# Revit family: vanity unit with 4 drawers for consoles with bowl
name_source: partatom
category: Furniture
units: mm (PartAtom-declared; Revit-internal decimal feet)

## family parameters
Always vertical = Yes
Cut with Voids When Loaded = No
OmniClass Number = 23.21.19.15.33.13
Room Calculation Point = No
Shared = Yes
Work Plane-Based = No

## types (48) — shared parameters
BIMOBJECT = Sanitary: Compound units
CATALOG = Hansgrohe
DESIGN = Germany
ETIM = EC011381 | Bathroom furniture set
IFC = Furnishing element
MASTERFORMAT = 12 35 30.23 | Bathroom Casework
Manufacturer = Hansgrohe
NBSYN = $BASENUMBER.-$ARTNR.-$OBERFLAECHE.-$SURFACE.-$LODLEVEL.
NN = Vanity Unit with 4 Drawers for consoles with bowl
OBJECTTYPE = Object (single object)
OMNICLASS = 23-21 19 15 33 13 | Residential Bathroom Specialty Casework
PRODUCTFAMILY = Xelu Q
PRODUCTGROUP = vanity unit
PRODUCTURL = https://pro.hansgrohe.com
REGIONSET = Worldwide
UNICLASS2015 = Pr_40_30_78_05 | Bathroom furniture
UNICLASS_2015_CODE = 40_30_78_05
UNIFORMATII = E2010 | Fixed Furnishings
UNSPSC = 56 | Furniture and Furnishings
etim7_EC011381 = EC011381

## per-type parameters (varying)
| type | ARTNR | BASENUMBER | GTINCODE | L | LINA | LODLEVEL | Model | NAME | NB | OBERFLAECHE | PERMALINK | SURFACE | WEIGHT |
| Vanity unit 1360_550 with 4 drawers for consoles with bowl-54086000-High Gloss White-CHROME-200 | 54086000 | Vanity unit 1360/550 with 4 drawers for consoles with bowl | 4059625456972 | 1360 | Vanity unit 1360/550 with 4 drawers for consoles with bowl-54086000-High Gloss White-CHROME-200 | 200 | Vanity unit 1360/550 with 4 drawers for consoles with bowl-54086000-High Gloss White-CHROME-200 | Xelu Q Vanity unit High Gloss White 1360/550 with 4 drawers for consoles with bowl | Vanity unit 1360/550 with 4 drawers for consoles with bowl-54086000-High Gloss White-CHROME-200 | High Gloss White | 54086XXX | CHROME | 55.8 |
| Vanity unit 1360_550 with 4 drawers for consoles with bowl-54086000-High Gloss White-CHROME-400 | 54086000 | Vanity unit 1360/550 with 4 drawers for consoles with bowl | 4059625456972 | 1360 | Vanity unit 1360/550 with 4 drawers for consoles with bowl-54086000-High Gloss White-CHROME-400 | 400 | Vanity unit 1360/550 with 4 drawers for consoles with bowl-54086000-High Gloss White-CHROME-400 | Xelu Q Vanity unit High Gloss White 1360/550 with 4 drawers for consoles with bowl | Vanity unit 1360/550 with 4 drawers for consoles with bowl-54086000-High Gloss White-CHROME-400 | High Gloss White | 54086XXX | CHROME | 55.8 |
| Vanity unit 1360_550 with 4 drawers for consoles with bowl-54086670-High Gloss White-MATT_BLACK-200 | 54086670 | Vanity unit 1360/550 with 4 drawers for consoles with bowl | 4059625456972 | 1360 | Vanity unit 1360/550 with 4 drawers for consoles with bowl-54086670-High Gloss White-MATT_BLACK-200 | 200 | Vanity unit 1360/550 with 4 drawers for consoles with bowl-54086670-High Gloss White-MATT_BLACK-200 | Xelu Q Vanity unit High Gloss White 1360/550 with 4 drawers for consoles with bowl | Vanity unit 1360/550 with 4 drawers for consoles with bowl-54086670-High Gloss White-MATT_BLACK-200 | High Gloss White | 54086XXX | MATT_BLACK | 55.8 |
| Vanity unit 1360_550 with 4 drawers for consoles with bowl-54086670-High Gloss White-MATT_BLACK-400 | 54086670 | Vanity unit 1360/550 with 4 drawers for consoles with bowl | 4059625456972 | 1360 | Vanity unit 1360/550 with 4 drawers for consoles with bowl-54086670-High Gloss White-MATT_BLACK-400 | 400 | Vanity unit 1360/550 with 4 drawers for consoles with bowl-54086670-High Gloss White-MATT_BLACK-400 | Xelu Q Vanity unit High Gloss White 1360/550 with 4 drawers for consoles with bowl | Vanity unit 1360/550 with 4 drawers for consoles with bowl-54086670-High Gloss White-MATT_BLACK-400 | High Gloss White | 54086XXX | MATT_BLACK | 55.8 |
| Vanity unit 1360_550 with 4 drawers for consoles with bowl-54086700-High Gloss White-MATT_WHITE-200 | 54086700 | Vanity unit 1360/550 with 4 drawers for consoles with bowl | 4059625456972 | 1360 | Vanity unit 1360/550 with 4 drawers for consoles with bowl-54086700-High Gloss White-MATT_WHITE-200 | 200 | Vanity unit 1360/550 with 4 drawers for consoles with bowl-54086700-High Gloss White-MATT_WHITE-200 | Xelu Q Vanity unit High Gloss White 1360/550 with 4 drawers for consoles with bowl | Vanity unit 1360/550 with 4 drawers for consoles with bowl-54086700-High Gloss White-MATT_WHITE-200 | High Gloss White | 54086XXX | MATT_WHITE | 55.8 |
| Vanity unit 1360_550 with 4 drawers for consoles with bowl-54086700-High Gloss White-MATT_WHITE-400 | 54086700 | Vanity unit 1360/550 with 4 drawers for consoles with bowl | 4059625456972 | 1360 | Vanity unit 1360/550 with 4 drawers for consoles with bowl-54086700-High Gloss White-MATT_WHITE-400 | 400 | Vanity unit 1360/550 with 4 drawers for consoles with bowl-54086700-High Gloss White-MATT_WHITE-400 | Xelu Q Vanity unit High Gloss White 1360/550 with 4 drawers for consoles with bowl | Vanity unit 1360/550 with 4 drawers for consoles with bowl-54086700-High Gloss White-MATT_WHITE-400 | High Gloss White | 54086XXX | MATT_WHITE | 55.8 |
| Vanity unit 1360_550 with 4 drawers for consoles with bowl-54087000-Diamond Matt Grey-CHROME-200 | 54087000 | Vanity unit 1360/550 with 4 drawers for consoles with bowl | 4059625456941 | 1360 | Vanity unit 1360/550 with 4 drawers for consoles with bowl-54087000-Diamond Matt Grey-CHROME-200 | 200 | Vanity unit 1360/550 with 4 drawers for consoles with bowl-54087000-Diamond Matt Grey-CHROME-200 | Xelu Q Vanity unit Diamond Matt Grey 1360/550 with 4 drawers for consoles with bowl | Vanity unit 1360/550 with 4 drawers for consoles with bowl-54087000-Diamond Matt Grey-CHROME-200 | Diamond Matt Grey | 54087XXX | CHROME | 55.8 |
| Vanity unit 1360_550 with 4 drawers for consoles with bowl-54087000-Diamond Matt Grey-CHROME-400 | 54087000 | Vanity unit 1360/550 with 4 drawers for consoles with bowl | 4059625456941 | 1360 | Vanity unit 1360/550 with 4 drawers for consoles with bowl-54087000-Diamond Matt Grey-CHROME-400 | 400 | Vanity unit 1360/550 with 4 drawers for consoles with bowl-54087000-Diamond Matt Grey-CHROME-400 | Xelu Q Vanity unit Diamond Matt Grey 1360/550 with 4 drawers for consoles with bowl | Vanity unit 1360/550 with 4 drawers for consoles with bowl-54087000-Diamond Matt Grey-CHROME-400 | Diamond Matt Grey | 54087XXX | CHROME | 55.8 |
| Vanity unit 1360_550 with 4 drawers for consoles with bowl-54087670-Diamond Matt Grey-MATT_BLACK-200 | 54087670 | Vanity unit 1360/550 with 4 drawers for consoles with bowl | 4059625456941 | 1360 | Vanity unit 1360/550 with 4 drawers for consoles with bowl-54087670-Diamond Matt Grey-MATT_BLACK-200 | 200 | Vanity unit 1360/550 with 4 drawers for consoles with bowl-54087670-Diamond Matt Grey-MATT_BLACK-200 | Xelu Q Vanity unit Diamond Matt Grey 1360/550 with 4 drawers for consoles with bowl | Vanity unit 1360/550 with 4 drawers for consoles with bowl-54087670-Diamond Matt Grey-MATT_BLACK-200 | Diamond Matt Grey | 54087XXX | MATT_BLACK | 55.8 |
| Vanity unit 1360_550 with 4 drawers for consoles with bowl-54087670-Diamond Matt Grey-MATT_BLACK-400 | 54087670 | Vanity unit 1360/550 with 4 drawers for consoles with bowl | 4059625456941 | 1360 | Vanity unit 1360/550 with 4 drawers for consoles with bowl-54087670-Diamond Matt Grey-MATT_BLACK-400 | 400 | Vanity unit 1360/550 with 4 drawers for consoles with bowl-54087670-Diamond Matt Grey-MATT_BLACK-400 | Xelu Q Vanity unit Diamond Matt Grey 1360/550 with 4 drawers for consoles with bowl | Vanity unit 1360/550 with 4 drawers for consoles with bowl-54087670-Diamond Matt Grey-MATT_BLACK-400 | Diamond Matt Grey | 54087XXX | MATT_BLACK | 55.8 |
| Vanity unit 1360_550 with 4 drawers for consoles with bowl-54087700-Diamond Matt Grey-MATT_WHITE-200 | 54087700 | Vanity unit 1360/550 with 4 drawers for consoles with bowl | 4059625456941 | 1360 | Vanity unit 1360/550 with 4 drawers for consoles with bowl-54087700-Diamond Matt Grey-MATT_WHITE-200 | 200 | Vanity unit 1360/550 with 4 drawers for consoles with bowl-54087700-Diamond Matt Grey-MATT_WHITE-200 | Xelu Q Vanity unit Diamond Matt Grey 1360/550 with 4 drawers for consoles with bowl | Vanity unit 1360/550 with 4 drawers for consoles with bowl-54087700-Diamond Matt Grey-MATT_WHITE-200 | Diamond Matt Grey | 54087XXX | MATT_WHITE | 55.8 |
| Vanity unit 1360_550 with 4 drawers for consoles with bowl-54087700-Diamond Matt Grey-MATT_WHITE-400 | 54087700 | Vanity unit 1360/550 with 4 drawers for consoles with bowl | 4059625456941 | 1360 | Vanity unit 1360/550 with 4 drawers for consoles with bowl-54087700-Diamond Matt Grey-MATT_WHITE-400 | 400 | Vanity unit 1360/550 with 4 drawers for consoles with bowl-54087700-Diamond Matt Grey-MATT_WHITE-400 | Xelu Q Vanity unit Diamond Matt Grey 1360/550 with 4 drawers for consoles with bowl | Vanity unit 1360/550 with 4 drawers for consoles with bowl-54087700-Diamond Matt Grey-MATT_WHITE-400 | Diamond Matt Grey | 54087XXX | MATT_WHITE | 55.8 |
| Vanity unit 1360_550 with 4 drawers for consoles with bowl-54088000-Natural Oak-CHROME-200 | 54088000 | Vanity unit 1360/550 with 4 drawers for consoles with bowl | 4059625456910 | 1360 | Vanity unit 1360/550 with 4 drawers for consoles with bowl-54088000-Natural Oak-CHROME-200 | 200 | Vanity unit 1360/550 with 4 drawers for consoles with bowl-54088000-Natural Oak-CHROME-200 | Xelu Q Vanity unit Natural Oak 1360/550 with 4 drawers for consoles with bowl | Vanity unit 1360/550 with 4 drawers for consoles with bowl-54088000-Natural Oak-CHROME-200 | Natural Oak | 54088XXX | CHROME | 55.8 |
| Vanity unit 1360_550 with 4 drawers for consoles with bowl-54088000-Natural Oak-CHROME-400 | 54088000 | Vanity unit 1360/550 with 4 drawers for consoles with bowl | 4059625456910 | 1360 | Vanity unit 1360/550 with 4 drawers for consoles with bowl-54088000-Natural Oak-CHROME-400 | 400 | Vanity unit 1360/550 with 4 drawers for consoles with bowl-54088000-Natural Oak-CHROME-400 | Xelu Q Vanity unit Natural Oak 1360/550 with 4 drawers for consoles with bowl | Vanity unit 1360/550 with 4 drawers for consoles with bowl-54088000-Natural Oak-CHROME-400 | Natural Oak | 54088XXX | CHROME | 55.8 |
| Vanity unit 1360_550 with 4 drawers for consoles with bowl-54088670-Natural Oak-MATT_BLACK-200 | 54088670 | Vanity unit 1360/550 with 4 drawers for consoles with bowl | 4059625456910 | 1360 | Vanity unit 1360/550 with 4 drawers for consoles with bowl-54088670-Natural Oak-MATT_BLACK-200 | 200 | Vanity unit 1360/550 with 4 drawers for consoles with bowl-54088670-Natural Oak-MATT_BLACK-200 | Xelu Q Vanity unit Natural Oak 1360/550 with 4 drawers for consoles with bowl | Vanity unit 1360/550 with 4 drawers for consoles with bowl-54088670-Natural Oak-MATT_BLACK-200 | Natural Oak | 54088XXX | MATT_BLACK | 55.8 |
| Vanity unit 1360_550 with 4 drawers for consoles with bowl-54088670-Natural Oak-MATT_BLACK-400 | 54088670 | Vanity unit 1360/550 with 4 drawers for consoles with bowl | 4059625456910 | 1360 | Vanity unit 1360/550 with 4 drawers for consoles with bowl-54088670-Natural Oak-MATT_BLACK-400 | 400 | Vanity unit 1360/550 with 4 drawers for consoles with bowl-54088670-Natural Oak-MATT_BLACK-400 | Xelu Q Vanity unit Natural Oak 1360/550 with 4 drawers for consoles with bowl | Vanity unit 1360/550 with 4 drawers for consoles with bowl-54088670-Natural Oak-MATT_BLACK-400 | Natural Oak | 54088XXX | MATT_BLACK | 55.8 |
| Vanity unit 1360_550 with 4 drawers for consoles with bowl-54088700-Natural Oak-MATT_WHITE-200 | 54088700 | Vanity unit 1360/550 with 4 drawers for consoles with bowl | 4059625456910 | 1360 | Vanity unit 1360/550 with 4 drawers for consoles with bowl-54088700-Natural Oak-MATT_WHITE-200 | 200 | Vanity unit 1360/550 with 4 drawers for consoles with bowl-54088700-Natural Oak-MATT_WHITE-200 | Xelu Q Vanity unit Natural Oak 1360/550 with 4 drawers for consoles with bowl | Vanity unit 1360/550 with 4 drawers for consoles with bowl-54088700-Natural Oak-MATT_WHITE-200 | Natural Oak | 54088XXX | MATT_WHITE | 55.8 |
| Vanity unit 1360_550 with 4 drawers for consoles with bowl-54088700-Natural Oak-MATT_WHITE-400 | 54088700 | Vanity unit 1360/550 with 4 drawers for consoles with bowl | 4059625456910 | 1360 | Vanity unit 1360/550 with 4 drawers for consoles with bowl-54088700-Natural Oak-MATT_WHITE-400 | 400 | Vanity unit 1360/550 with 4 drawers for consoles with bowl-54088700-Natural Oak-MATT_WHITE-400 | Xelu Q Vanity unit Natural Oak 1360/550 with 4 drawers for consoles with bowl | Vanity unit 1360/550 with 4 drawers for consoles with bowl-54088700-Natural Oak-MATT_WHITE-400 | Natural Oak | 54088XXX | MATT_WHITE | 55.8 |
| Vanity unit 1360_550 with 4 drawers for consoles with bowl-54089000-Dark Walnut-CHROME-200 | 54089000 | Vanity unit 1360/550 with 4 drawers for consoles with bowl | 4059625456880 | 1360 | Vanity unit 1360/550 with 4 drawers for consoles with bowl-54089000-Dark Walnut-CHROME-200 | 200 | Vanity unit 1360/550 with 4 drawers for consoles with bowl-54089000-Dark Walnut-CHROME-200 | Xelu Q Vanity unit Dark Walnut 1360/550 with 4 drawers for consoles with bowl | Vanity unit 1360/550 with 4 drawers for consoles with bowl-54089000-Dark Walnut-CHROME-200 | Dark Walnut | 54089XXX | CHROME | 55.8 |
| Vanity unit 1360_550 with 4 drawers for consoles with bowl-54089000-Dark Walnut-CHROME-400 | 54089000 | Vanity unit 1360/550 with 4 drawers for consoles with bowl | 4059625456880 | 1360 | Vanity unit 1360/550 with 4 drawers for consoles with bowl-54089000-Dark Walnut-CHROME-400 | 400 | Vanity unit 1360/550 with 4 drawers for consoles with bowl-54089000-Dark Walnut-CHROME-400 | Xelu Q Vanity unit Dark Walnut 1360/550 with 4 drawers for consoles with bowl | Vanity unit 1360/550 with 4 drawers for consoles with bowl-54089000-Dark Walnut-CHROME-400 | Dark Walnut | 54089XXX | CHROME | 55.8 |
| Vanity unit 1360_550 with 4 drawers for consoles with bowl-54089670-Dark Walnut-MATT_BLACK-200 | 54089670 | Vanity unit 1360/550 with 4 drawers for consoles with bowl | 4059625456880 | 1360 | Vanity unit 1360/550 with 4 drawers for consoles with bowl-54089670-Dark Walnut-MATT_BLACK-200 | 200 | Vanity unit 1360/550 with 4 drawers for consoles with bowl-54089670-Dark Walnut-MATT_BLACK-200 | Xelu Q Vanity unit Dark Walnut 1360/550 with 4 drawers for consoles with bowl | Vanity unit 1360/550 with 4 drawers for consoles with bowl-54089670-Dark Walnut-MATT_BLACK-200 | Dark Walnut | 54089XXX | MATT_BLACK | 55.8 |
| Vanity unit 1360_550 with 4 drawers for consoles with bowl-54089670-Dark Walnut-MATT_BLACK-400 | 54089670 | Vanity unit 1360/550 with 4 drawers for consoles with bowl | 4059625456880 | 1360 | Vanity unit 1360/550 with 4 drawers for consoles with bowl-54089670-Dark Walnut-MATT_BLACK-400 | 400 | Vanity unit 1360/550 with 4 drawers for consoles with bowl-54089670-Dark Walnut-MATT_BLACK-400 | Xelu Q Vanity unit Dark Walnut 1360/550 with 4 drawers for consoles with bowl | Vanity unit 1360/550 with 4 drawers for consoles with bowl-54089670-Dark Walnut-MATT_BLACK-400 | Dark Walnut | 54089XXX | MATT_BLACK | 55.8 |
| Vanity unit 1360_550 with 4 drawers for consoles with bowl-54089700-Dark Walnut-MATT_WHITE-200 | 54089700 | Vanity unit 1360/550 with 4 drawers for consoles with bowl | 4059625456880 | 1360 | Vanity unit 1360/550 with 4 drawers for consoles with bowl-54089700-Dark Walnut-MATT_WHITE-200 | 200 | Vanity unit 1360/550 with 4 drawers for consoles with bowl-54089700-Dark Walnut-MATT_WHITE-200 | Xelu Q Vanity unit Dark Walnut 1360/550 with 4 drawers for consoles with bowl | Vanity unit 1360/550 with 4 drawers for consoles with bowl-54089700-Dark Walnut-MATT_WHITE-200 | Dark Walnut | 54089XXX | MATT_WHITE | 55.8 |
| Vanity unit 1360_550 with 4 drawers for consoles with bowl-54089700-Dark Walnut-MATT_WHITE-400 | 54089700 | Vanity unit 1360/550 with 4 drawers for consoles with bowl | 4059625456880 | 1360 | Vanity unit 1360/550 with 4 drawers for consoles with bowl-54089700-Dark Walnut-MATT_WHITE-400 | 400 | Vanity unit 1360/550 with 4 drawers for consoles with bowl-54089700-Dark Walnut-MATT_WHITE-400 | Xelu Q Vanity unit Dark Walnut 1360/550 with 4 drawers for consoles with bowl | Vanity unit 1360/550 with 4 drawers for consoles with bowl-54089700-Dark Walnut-MATT_WHITE-400 | Dark Walnut | 54089XXX | MATT_WHITE | 55.8 |
| Vanity unit 1560_550 with 4 drawers for consoles with bowl-54090000-High Gloss White-CHROME-200 | 54090000 | Vanity unit 1560/550 with 4 drawers for consoles with bowl | 4059625456859 | 1560 | Vanity unit 1560/550 with 4 drawers for consoles with bowl-54090000-High Gloss White-CHROME-200 | 200 | Vanity unit 1560/550 with 4 drawers for consoles with bowl-54090000-High Gloss White-CHROME-200 | Xelu Q Vanity unit High Gloss White 1560/550 with 4 drawers for consoles with bowl | Vanity unit 1560/550 with 4 drawers for consoles with bowl-54090000-High Gloss White-CHROME-200 | High Gloss White | 54090XXX | CHROME | 61 |
| Vanity unit 1560_550 with 4 drawers for consoles with bowl-54090000-High Gloss White-CHROME-400 | 54090000 | Vanity unit 1560/550 with 4 drawers for consoles with bowl | 4059625456859 | 1560 | Vanity unit 1560/550 with 4 drawers for consoles with bowl-54090000-High Gloss White-CHROME-400 | 400 | Vanity unit 1560/550 with 4 drawers for consoles with bowl-54090000-High Gloss White-CHROME-400 | Xelu Q Vanity unit High Gloss White 1560/550 with 4 drawers for consoles with bowl | Vanity unit 1560/550 with 4 drawers for consoles with bowl-54090000-High Gloss White-CHROME-400 | High Gloss White | 54090XXX | CHROME | 61 |
| Vanity unit 1560_550 with 4 drawers for consoles with bowl-54090670-High Gloss White-MATT_BLACK-200 | 54090670 | Vanity unit 1560/550 with 4 drawers for consoles with bowl | 4059625456859 | 1560 | Vanity unit 1560/550 with 4 drawers for consoles with bowl-54090670-High Gloss White-MATT_BLACK-200 | 200 | Vanity unit 1560/550 with 4 drawers for consoles with bowl-54090670-High Gloss White-MATT_BLACK-200 | Xelu Q Vanity unit High Gloss White 1560/550 with 4 drawers for consoles with bowl | Vanity unit 1560/550 with 4 drawers for consoles with bowl-54090670-High Gloss White-MATT_BLACK-200 | High Gloss White | 54090XXX | MATT_BLACK | 61 |
| Vanity unit 1560_550 with 4 drawers for consoles with bowl-54090670-High Gloss White-MATT_BLACK-400 | 54090670 | Vanity unit 1560/550 with 4 drawers for consoles with bowl | 4059625456859 | 1560 | Vanity unit 1560/550 with 4 drawers for consoles with bowl-54090670-High Gloss White-MATT_BLACK-400 | 400 | Vanity unit 1560/550 with 4 drawers for consoles with bowl-54090670-High Gloss White-MATT_BLACK-400 | Xelu Q Vanity unit High Gloss White 1560/550 with 4 drawers for consoles with bowl | Vanity unit 1560/550 with 4 drawers for consoles with bowl-54090670-High Gloss White-MATT_BLACK-400 | High Gloss White | 54090XXX | MATT_BLACK | 61 |
| Vanity unit 1560_550 with 4 drawers for consoles with bowl-54090700-High Gloss White-MATT_WHITE-200 | 54090700 | Vanity unit 1560/550 with 4 drawers for consoles with bowl | 4059625456859 | 1560 | Vanity unit 1560/550 with 4 drawers for consoles with bowl-54090700-High Gloss White-MATT_WHITE-200 | 200 | Vanity unit 1560/550 with 4 drawers for consoles with bowl-54090700-High Gloss White-MATT_WHITE-200 | Xelu Q Vanity unit High Gloss White 1560/550 with 4 drawers for consoles with bowl | Vanity unit 1560/550 with 4 drawers for consoles with bowl-54090700-High Gloss White-MATT_WHITE-200 | High Gloss White | 54090XXX | MATT_WHITE | 61 |
| Vanity unit 1560_550 with 4 drawers for consoles with bowl-54090700-High Gloss White-MATT_WHITE-400 | 54090700 | Vanity unit 1560/550 with 4 drawers for consoles with bowl | 4059625456859 | 1560 | Vanity unit 1560/550 with 4 drawers for consoles with bowl-54090700-High Gloss White-MATT_WHITE-400 | 400 | Vanity unit 1560/550 with 4 drawers for consoles with bowl-54090700-High Gloss White-MATT_WHITE-400 | Xelu Q Vanity unit High Gloss White 1560/550 with 4 drawers for consoles with bowl | Vanity unit 1560/550 with 4 drawers for consoles with bowl-54090700-High Gloss White-MATT_WHITE-400 | High Gloss White | 54090XXX | MATT_WHITE | 61 |
| Vanity unit 1560_550 with 4 drawers for consoles with bowl-54091000-Diamond Matt Grey-CHROME-200 | 54091000 | Vanity unit 1560/550 with 4 drawers for consoles with bowl | 4059625457221 | 1560 | Vanity unit 1560/550 with 4 drawers for consoles with bowl-54091000-Diamond Matt Grey-CHROME-200 | 200 | Vanity unit 1560/550 with 4 drawers for consoles with bowl-54091000-Diamond Matt Grey-CHROME-200 | Xelu Q Vanity unit Diamond Matt Grey 1560/550 with 4 drawers for consoles with bowl | Vanity unit 1560/550 with 4 drawers for consoles with bowl-54091000-Diamond Matt Grey-CHROME-200 | Diamond Matt Grey | 54091XXX | CHROME | 61 |
| Vanity unit 1560_550 with 4 drawers for consoles with bowl-54091000-Diamond Matt Grey-CHROME-400 | 54091000 | Vanity unit 1560/550 with 4 drawers for consoles with bowl | 4059625457221 | 1560 | Vanity unit 1560/550 with 4 drawers for consoles with bowl-54091000-Diamond Matt Grey-CHROME-400 | 400 | Vanity unit 1560/550 with 4 drawers for consoles with bowl-54091000-Diamond Matt Grey-CHROME-400 | Xelu Q Vanity unit Diamond Matt Grey 1560/550 with 4 drawers for consoles with bowl | Vanity unit 1560/550 with 4 drawers for consoles with bowl-54091000-Diamond Matt Grey-CHROME-400 | Diamond Matt Grey | 54091XXX | CHROME | 61 |
| Vanity unit 1560_550 with 4 drawers for consoles with bowl-54091670-Diamond Matt Grey-MATT_BLACK-200 | 54091670 | Vanity unit 1560/550 with 4 drawers for consoles with bowl | 4059625457221 | 1560 | Vanity unit 1560/550 with 4 drawers for consoles with bowl-54091670-Diamond Matt Grey-MATT_BLACK-200 | 200 | Vanity unit 1560/550 with 4 drawers for consoles with bowl-54091670-Diamond Matt Grey-MATT_BLACK-200 | Xelu Q Vanity unit Diamond Matt Grey 1560/550 with 4 drawers for consoles with bowl | Vanity unit 1560/550 with 4 drawers for consoles with bowl-54091670-Diamond Matt Grey-MATT_BLACK-200 | Diamond Matt Grey | 54091XXX | MATT_BLACK | 61 |
| Vanity unit 1560_550 with 4 drawers for consoles with bowl-54091670-Diamond Matt Grey-MATT_BLACK-400 | 54091670 | Vanity unit 1560/550 with 4 drawers for consoles with bowl | 4059625457221 | 1560 | Vanity unit 1560/550 with 4 drawers for consoles with bowl-54091670-Diamond Matt Grey-MATT_BLACK-400 | 400 | Vanity unit 1560/550 with 4 drawers for consoles with bowl-54091670-Diamond Matt Grey-MATT_BLACK-400 | Xelu Q Vanity unit Diamond Matt Grey 1560/550 with 4 drawers for consoles with bowl | Vanity unit 1560/550 with 4 drawers for consoles with bowl-54091670-Diamond Matt Grey-MATT_BLACK-400 | Diamond Matt Grey | 54091XXX | MATT_BLACK | 61 |
| Vanity unit 1560_550 with 4 drawers for consoles with bowl-54091700-Diamond Matt Grey-MATT_WHITE-200 | 54091700 | Vanity unit 1560/550 with 4 drawers for consoles with bowl | 4059625457221 | 1560 | Vanity unit 1560/550 with 4 drawers for consoles with bowl-54091700-Diamond Matt Grey-MATT_WHITE-200 | 200 | Vanity unit 1560/550 with 4 drawers for consoles with bowl-54091700-Diamond Matt Grey-MATT_WHITE-200 | Xelu Q Vanity unit Diamond Matt Grey 1560/550 with 4 drawers for consoles with bowl | Vanity unit 1560/550 with 4 drawers for consoles with bowl-54091700-Diamond Matt Grey-MATT_WHITE-200 | Diamond Matt Grey | 54091XXX | MATT_WHITE | 61 |
| Vanity unit 1560_550 with 4 drawers for consoles with bowl-54091700-Diamond Matt Grey-MATT_WHITE-400 | 54091700 | Vanity unit 1560/550 with 4 drawers for consoles with bowl | 4059625457221 | 1560 | Vanity unit 1560/550 with 4 drawers for consoles with bowl-54091700-Diamond Matt Grey-MATT_WHITE-400 | 400 | Vanity unit 1560/550 with 4 drawers for consoles with bowl-54091700-Diamond Matt Grey-MATT_WHITE-400 | Xelu Q Vanity unit Diamond Matt Grey 1560/550 with 4 drawers for consoles with bowl | Vanity unit 1560/550 with 4 drawers for consoles with bowl-54091700-Diamond Matt Grey-MATT_WHITE-400 | Diamond Matt Grey | 54091XXX | MATT_WHITE | 61 |
| Vanity unit 1560_550 with 4 drawers for consoles with bowl-54092000-Natural Oak-CHROME-200 | 54092000 | Vanity unit 1560/550 with 4 drawers for consoles with bowl | 4059625457191 | 1560 | Vanity unit 1560/550 with 4 drawers for consoles with bowl-54092000-Natural Oak-CHROME-200 | 200 | Vanity unit 1560/550 with 4 drawers for consoles with bowl-54092000-Natural Oak-CHROME-200 | Xelu Q Vanity unit Natural Oak 1560/550 with 4 drawers for consoles with bowl | Vanity unit 1560/550 with 4 drawers for consoles with bowl-54092000-Natural Oak-CHROME-200 | Natural Oak | 54092XXX | CHROME | 61 |
| Vanity unit 1560_550 with 4 drawers for consoles with bowl-54092000-Natural Oak-CHROME-400 | 54092000 | Vanity unit 1560/550 with 4 drawers for consoles with bowl | 4059625457191 | 1560 | Vanity unit 1560/550 with 4 drawers for consoles with bowl-54092000-Natural Oak-CHROME-400 | 400 | Vanity unit 1560/550 with 4 drawers for consoles with bowl-54092000-Natural Oak-CHROME-400 | Xelu Q Vanity unit Natural Oak 1560/550 with 4 drawers for consoles with bowl | Vanity unit 1560/550 with 4 drawers for consoles with bowl-54092000-Natural Oak-CHROME-400 | Natural Oak | 54092XXX | CHROME | 61 |
| Vanity unit 1560_550 with 4 drawers for consoles with bowl-54092670-Natural Oak-MATT_BLACK-200 | 54092670 | Vanity unit 1560/550 with 4 drawers for consoles with bowl | 4059625457191 | 1560 | Vanity unit 1560/550 with 4 drawers for consoles with bowl-54092670-Natural Oak-MATT_BLACK-200 | 200 | Vanity unit 1560/550 with 4 drawers for consoles with bowl-54092670-Natural Oak-MATT_BLACK-200 | Xelu Q Vanity unit Natural Oak 1560/550 with 4 drawers for consoles with bowl | Vanity unit 1560/550 with 4 drawers for consoles with bowl-54092670-Natural Oak-MATT_BLACK-200 | Natural Oak | 54092XXX | MATT_BLACK | 61 |
| Vanity unit 1560_550 with 4 drawers for consoles with bowl-54092670-Natural Oak-MATT_BLACK-400 | 54092670 | Vanity unit 1560/550 with 4 drawers for consoles with bowl | 4059625457191 | 1560 | Vanity unit 1560/550 with 4 drawers for consoles with bowl-54092670-Natural Oak-MATT_BLACK-400 | 400 | Vanity unit 1560/550 with 4 drawers for consoles with bowl-54092670-Natural Oak-MATT_BLACK-400 | Xelu Q Vanity unit Natural Oak 1560/550 with 4 drawers for consoles with bowl | Vanity unit 1560/550 with 4 drawers for consoles with bowl-54092670-Natural Oak-MATT_BLACK-400 | Natural Oak | 54092XXX | MATT_BLACK | 61 |
| Vanity unit 1560_550 with 4 drawers for consoles with bowl-54092700-Natural Oak-MATT_WHITE-200 | 54092700 | Vanity unit 1560/550 with 4 drawers for consoles with bowl | 4059625457191 | 1560 | Vanity unit 1560/550 with 4 drawers for consoles with bowl-54092700-Natural Oak-MATT_WHITE-200 | 200 | Vanity unit 1560/550 with 4 drawers for consoles with bowl-54092700-Natural Oak-MATT_WHITE-200 | Xelu Q Vanity unit Natural Oak 1560/550 with 4 drawers for consoles with bowl | Vanity unit 1560/550 with 4 drawers for consoles with bowl-54092700-Natural Oak-MATT_WHITE-200 | Natural Oak | 54092XXX | MATT_WHITE | 61 |
| Vanity unit 1560_550 with 4 drawers for consoles with bowl-54092700-Natural Oak-MATT_WHITE-400 | 54092700 | Vanity unit 1560/550 with 4 drawers for consoles with bowl | 4059625457191 | 1560 | Vanity unit 1560/550 with 4 drawers for consoles with bowl-54092700-Natural Oak-MATT_WHITE-400 | 400 | Vanity unit 1560/550 with 4 drawers for consoles with bowl-54092700-Natural Oak-MATT_WHITE-400 | Xelu Q Vanity unit Natural Oak 1560/550 with 4 drawers for consoles with bowl | Vanity unit 1560/550 with 4 drawers for consoles with bowl-54092700-Natural Oak-MATT_WHITE-400 | Natural Oak | 54092XXX | MATT_WHITE | 61 |
| Vanity unit 1560_550 with 4 drawers for consoles with bowl-54093000-Dark Walnut-CHROME-200 | 54093000 | Vanity unit 1560/550 with 4 drawers for consoles with bowl | 4059625457160 | 1560 | Vanity unit 1560/550 with 4 drawers for consoles with bowl-54093000-Dark Walnut-CHROME-200 | 200 | Vanity unit 1560/550 with 4 drawers for consoles with bowl-54093000-Dark Walnut-CHROME-200 | Xelu Q Vanity unit Dark Walnut 1560/550 with 4 drawers for consoles with bowl | Vanity unit 1560/550 with 4 drawers for consoles with bowl-54093000-Dark Walnut-CHROME-200 | Dark Walnut | 54093XXX | CHROME | 61 |
| Vanity unit 1560_550 with 4 drawers for consoles with bowl-54093000-Dark Walnut-CHROME-400 | 54093000 | Vanity unit 1560/550 with 4 drawers for consoles with bowl | 4059625457160 | 1560 | Vanity unit 1560/550 with 4 drawers for consoles with bowl-54093000-Dark Walnut-CHROME-400 | 400 | Vanity unit 1560/550 with 4 drawers for consoles with bowl-54093000-Dark Walnut-CHROME-400 | Xelu Q Vanity unit Dark Walnut 1560/550 with 4 drawers for consoles with bowl | Vanity unit 1560/550 with 4 drawers for consoles with bowl-54093000-Dark Walnut-CHROME-400 | Dark Walnut | 54093XXX | CHROME | 61 |
| Vanity unit 1560_550 with 4 drawers for consoles with bowl-54093670-Dark Walnut-MATT_BLACK-200 | 54093670 | Vanity unit 1560/550 with 4 drawers for consoles with bowl | 4059625457160 | 1560 | Vanity unit 1560/550 with 4 drawers for consoles with bowl-54093670-Dark Walnut-MATT_BLACK-200 | 200 | Vanity unit 1560/550 with 4 drawers for consoles with bowl-54093670-Dark Walnut-MATT_BLACK-200 | Xelu Q Vanity unit Dark Walnut 1560/550 with 4 drawers for consoles with bowl | Vanity unit 1560/550 with 4 drawers for consoles with bowl-54093670-Dark Walnut-MATT_BLACK-200 | Dark Walnut | 54093XXX | MATT_BLACK | 61 |
| Vanity unit 1560_550 with 4 drawers for consoles with bowl-54093670-Dark Walnut-MATT_BLACK-400 | 54093670 | Vanity unit 1560/550 with 4 drawers for consoles with bowl | 4059625457160 | 1560 | Vanity unit 1560/550 with 4 drawers for consoles with bowl-54093670-Dark Walnut-MATT_BLACK-400 | 400 | Vanity unit 1560/550 with 4 drawers for consoles with bowl-54093670-Dark Walnut-MATT_BLACK-400 | Xelu Q Vanity unit Dark Walnut 1560/550 with 4 drawers for consoles with bowl | Vanity unit 1560/550 with 4 drawers for consoles with bowl-54093670-Dark Walnut-MATT_BLACK-400 | Dark Walnut | 54093XXX | MATT_BLACK | 61 |
| Vanity unit 1560_550 with 4 drawers for consoles with bowl-54093700-Dark Walnut-MATT_WHITE-200 | 54093700 | Vanity unit 1560/550 with 4 drawers for consoles with bowl | 4059625457160 | 1560 | Vanity unit 1560/550 with 4 drawers for consoles with bowl-54093700-Dark Walnut-MATT_WHITE-200 | 200 | Vanity unit 1560/550 with 4 drawers for consoles with bowl-54093700-Dark Walnut-MATT_WHITE-200 | Xelu Q Vanity unit Dark Walnut 1560/550 with 4 drawers for consoles with bowl | Vanity unit 1560/550 with 4 drawers for consoles with bowl-54093700-Dark Walnut-MATT_WHITE-200 | Dark Walnut | 54093XXX | MATT_WHITE | 61 |
| Vanity unit 1560_550 with 4 drawers for consoles with bowl-54093700-Dark Walnut-MATT_WHITE-400 | 54093700 | Vanity unit 1560/550 with 4 drawers for consoles with bowl | 4059625457160 | 1560 | Vanity unit 1560/550 with 4 drawers for consoles with bowl-54093700-Dark Walnut-MATT_WHITE-400 | 400 | Vanity unit 1560/550 with 4 drawers for consoles with bowl-54093700-Dark Walnut-MATT_WHITE-400 | Xelu Q Vanity unit Dark Walnut 1560/550 with 4 drawers for consoles with bowl | Vanity unit 1560/550 with 4 drawers for consoles with bowl-54093700-Dark Walnut-MATT_WHITE-400 | Dark Walnut | 54093XXX | MATT_WHITE | 61 |

type visibility flags: 48 boolean params named "<type name>_RX0RY0RZ0TX0TY0TZ0_V" — each type sets only its own to Yes (folded from table)

## geometry (parser evidence)
native form markers: Sweep x99
no freeform markers — native parametric forms only
